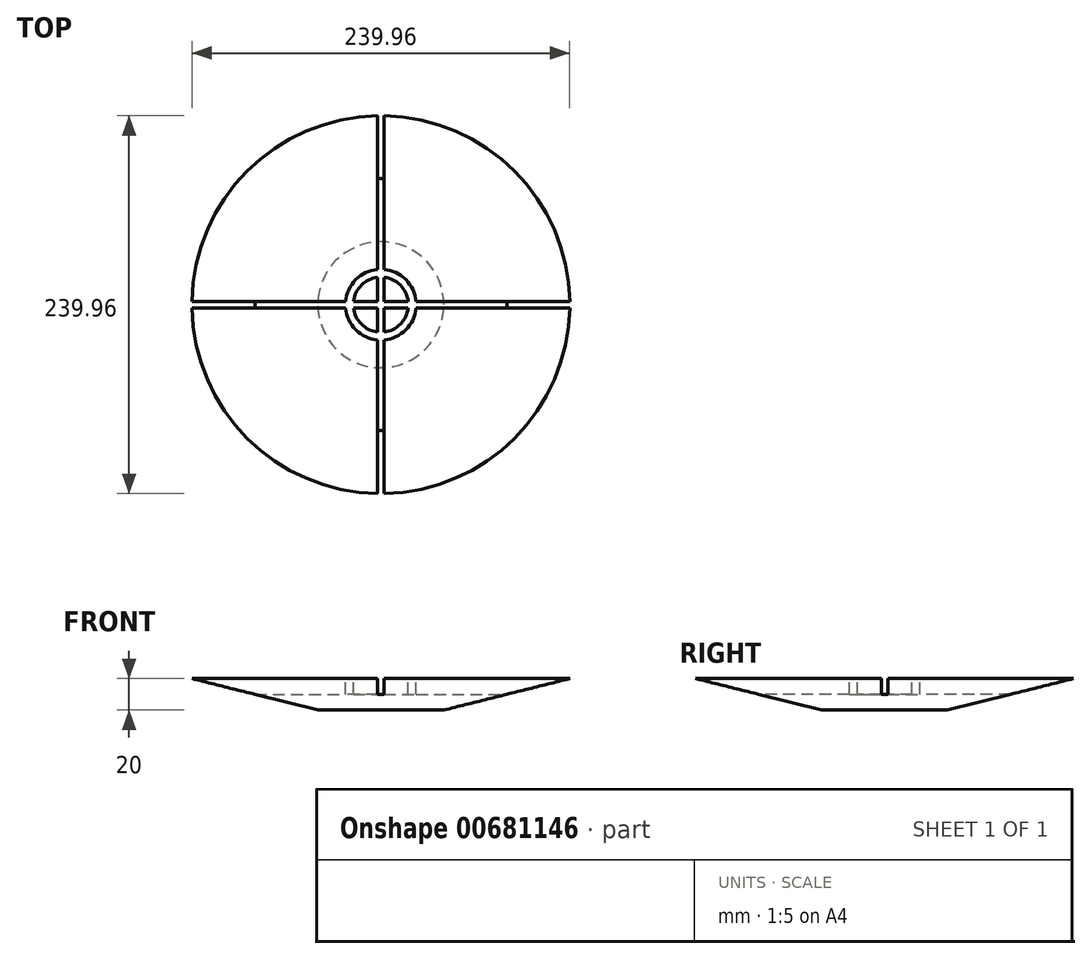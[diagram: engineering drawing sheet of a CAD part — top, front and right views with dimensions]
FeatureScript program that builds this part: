
annotation { "Feature Type Name" : "Feature", "Feature Type Description" : "" }
export const myFeature = defineFeature(function(context is Context, id is Id, definition is map)
    precondition{}
    {
        {
            var Q0;
            Q0=qCreatedBy(makeId("Front.planeOp"),FACE);
            var sketch = newSketch(context, id + "F0", { "sketchPlane" : qUnion([Q0])});
            skLineSegment(sketch, "E0", {"start": v(0, 0) * mm, "end": v(40, 0) * mm});
            skLineSegment(sketch, "E1", {"start": v(40, 0) * mm, "end": v(120, 20) * mm});
            skLineSegment(sketch, "E2", {"start": v(120, 20) * mm, "end": v(0, 20) * mm});
            skLineSegment(sketch, "E3", {"start": v(0, 20) * mm, "end": v(0, 0) * mm});
            skSolve(sketch);
        }
        {
            var Q0;
            Q0 = qSketchRegion(id + "F0", true);
            var Q1;
            Q1=sQuery(id+"F0.wireOp",EDGE,"E3");
            revolve(context, id + "F1", {"entities" : qUnion([Q0]), "axis" : qUnion([Q1]), "revolveType" : RevolveType.FULL});
        }
        {
            var Q0;
            Q0=makeQuery(id+"F1.opRevolve","SWEPT_FACE",FACE,{"disambiguationData":[OSD([sQuery(id+"F0.wireOp",EDGE,"E2")])]});
            var sketch = newSketch(context, id + "F2", { "sketchPlane" : qUnion([Q0])});
            skCircle(sketch, "E4", {"center": v(0, 0) * mm, "radius": 17.5 * mm});
            skCircle(sketch, "E5", {"center": v(0, 0) * mm, "radius": 22.5 * mm});
            skSolve(sketch);
        }
        {
            var Q0;
            Q0 = qSketchRegion(id + "F2", true);
            extrude(context, id + "F3", {"entities" : qUnion([Q0]), "operationType" : NewBodyOperationType.REMOVE, "oppositeDirection" : true, "depth" : 10 * mm, "offsetDistance" : 25.4 * mm});
        }
        {
            var Q0;
            Q0=makeQuery(id+"F3.boolean.opBoolean","SPLIT",FACE,{"disambiguationData":[TD([makeQuery(id+"F1.opRevolve","SWEPT_FACE",FACE,{"disambiguationData":[OSD([sQuery(id+"F0.wireOp",EDGE,"E1")])]})])],"derivedFrom":makeQuery(id+"F1.opRevolve","SWEPT_FACE",FACE,{"disambiguationData":[OSD([sQuery(id+"F0.wireOp",EDGE,"E2")])]})});
            var sketch = newSketch(context, id + "F4", { "sketchPlane" : qUnion([Q0])});
            skLineSegment(sketch, "E6", {"start": v(0, 120) * mm, "end": v(0, -120) * mm, "construction": true});
            skLineSegment(sketch, "E7", {"start": v(-120, 0) * mm, "end": v(120, 0) * mm, "construction": true});
            skLineSegment(sketch, "E8", {"start": v(2, 119.98) * mm, "end": v(2, -119.98) * mm});
            skLineSegment(sketch, "E9.MirrorCS", {"start": v(-2, 119.98) * mm, "end": v(-2, -119.98) * mm});
            skLineSegment(sketch, "E10", {"start": v(-119.98, -2) * mm, "end": v(119.98, -2) * mm});
            skLineSegment(sketch, "E11.MirrorCS", {"start": v(-119.98, 2) * mm, "end": v(119.98, 2) * mm});
            skArc(sketch, "E12", {"start": v(-119.98, 2) * mm, "mid": v(-120, 0) * mm, "end": v(-119.98, -2) * mm});
            skArc(sketch, "E13.trimOffspring", {"start": v(2, 119.98) * mm, "mid": v(0, 120) * mm, "end": v(-2, 119.98) * mm});
            skArc(sketch, "E14.trimOffspring", {"start": v(119.98, -2) * mm, "mid": v(120, 0) * mm, "end": v(119.98, 2) * mm});
            skArc(sketch, "E15.trimOffspring", {"start": v(-2, -119.98) * mm, "mid": v(0, -120) * mm, "end": v(2, -119.98) * mm});
            skSolve(sketch);
        }
        {
            var Q0;
            Q0 = qSketchRegion(id + "F4", true);
            extrude(context, id + "F5", {"entities" : qUnion([Q0]), "operationType" : NewBodyOperationType.REMOVE, "oppositeDirection" : true, "depth" : 10 * mm, "offsetDistance" : 25.4 * mm});
        }
    });
